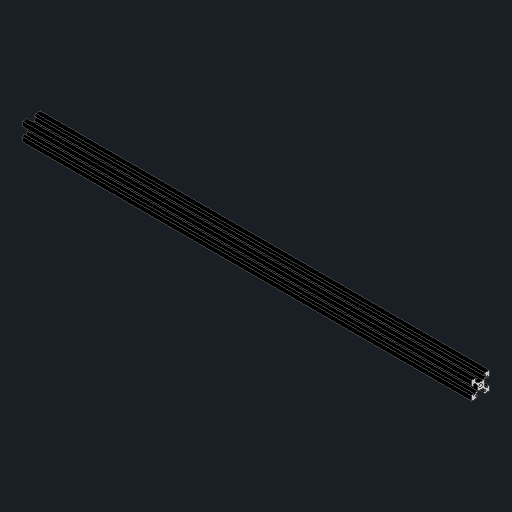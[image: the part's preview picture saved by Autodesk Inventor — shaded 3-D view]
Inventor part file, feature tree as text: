
AUTODESK INVENTOR PART (.ipt)
format: ipt  version: 2025.1 (Build 291241000, 241)  size: 280,576 bytes
history: native  units: mm
features: sketch x2, extrude x1
ambient origin geometry x8: Origin, YZ Plane, XZ Plane, XY Plane, X Axis, Y Axis, Z Axis, Center Point
bodies: Solid1 (feature_tree)
feature tree (3):
  extrude  "Extrusion1"  Depth=19.9mm
  sketch  "Sketch1"  dims[d0=19.9mm d1=19.9mm]
  sketch  "Sketch Circular Pattern1"  dims[d2=1.8mm d3=6.25mm d4=5.7mm d5=0.75mm d6=45.0deg d7=4.0mm d8=1.8mm d9=45.0deg d10=1.65mm d11=40.0mm d13=360.0deg d15=500.0mm d16=0.0mm]
